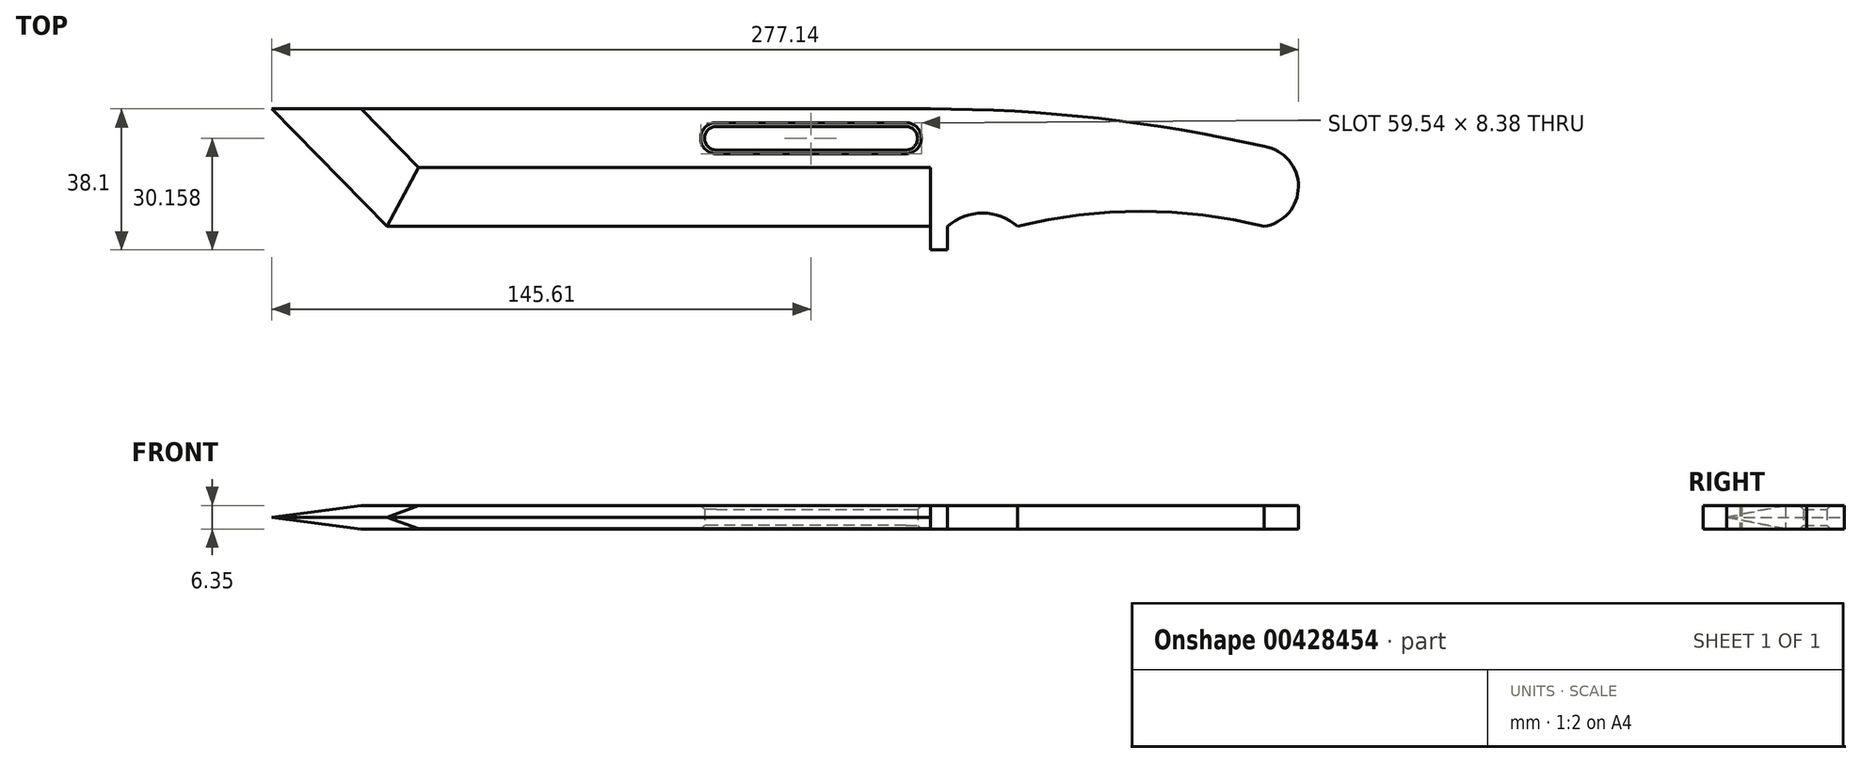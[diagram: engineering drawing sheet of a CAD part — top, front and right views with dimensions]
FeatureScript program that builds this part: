
annotation { "Feature Type Name" : "Feature", "Feature Type Description" : "" }
export const myFeature = defineFeature(function(context is Context, id is Id, definition is map)
    precondition{}
    {
        {
            var Q0;
            Q0=qCreatedBy(makeId("Top.planeOp"),FACE);
            var sketch = newSketch(context, id + "F0", { "sketchPlane" : qUnion([Q0])});
            skLineSegment(sketch, "E0", {"start": v(-135, 10.18) * mm, "end": v(-103.87, -21.57) * mm});
            skLineSegment(sketch, "E1", {"start": v(-135, 10.18) * mm, "end": v(42.8, 10.18) * mm});
            skLineSegment(sketch, "E2", {"start": v(-103.87, -21.57) * mm, "end": v(42.8, -21.57) * mm});
            skLineSegment(sketch, "E3", {"start": v(-103.87, -21.57) * mm, "end": v(-95.34, -5.7) * mm});
            skPoint(sketch, "E3.endSnap0", {"position": v(42.8, -5.7) * mm});
            skLineSegment(sketch, "E4", {"start": v(-95.34, -5.7) * mm, "end": v(42.8, -5.7) * mm});
            skLineSegment(sketch, "E5", {"start": v(-95.34, -5.7) * mm, "end": v(-110.83, 10.18) * mm});
            skLineSegment(sketch, "E6", {"start": v(42.8, -5.7) * mm, "end": v(42.8, -27.92) * mm});
            skLineSegment(sketch, "E7", {"start": v(42.8, -27.92) * mm, "end": v(47.45, -27.92) * mm});
            skLineSegment(sketch, "E8", {"start": v(47.45, -27.92) * mm, "end": v(47.45, -21.57) * mm});
            skArc(sketch, "E9", {"start": v(66.35, -21.57) * mm, "mid": v(56.9, -17.97) * mm, "end": v(47.45, -21.57) * mm});
            skArc(sketch, "E10", {"start": v(132.84, -21.57) * mm, "mid": v(99.6, -17.5) * mm, "end": v(66.35, -21.57) * mm});
            skArc(sketch, "E11", {"start": v(132.97, 0) * mm, "mid": v(88.17, 7.62) * mm, "end": v(42.8, 10.18) * mm});
            skArc(sketch, "E12", {"start": v(132.84, -21.57) * mm, "mid": v(142.14, -10.84) * mm, "end": v(132.97, 0) * mm});
            skLineSegment(sketch, "E13", {"start": v(36.19, 2.24) * mm, "end": v(-14.97, 2.24) * mm});
            skArc(sketch, "E14.0.startCap", {"start": v(36.19, 5.41) * mm, "mid": v(39.36, 2.24) * mm, "end": v(36.19, -0.94) * mm});
            skArc(sketch, "E14.0.endCap", {"start": v(-14.97, -0.94) * mm, "mid": v(-18.14, 2.24) * mm, "end": v(-14.97, 5.41) * mm});
            skLineSegment(sketch, "E14.0.left", {"start": v(36.19, -0.94) * mm, "end": v(-14.97, -0.94) * mm});
            skLineSegment(sketch, "E14.0.right", {"start": v(36.19, 5.41) * mm, "end": v(-14.97, 5.41) * mm});
            skSolve(sketch);
        }
        {
            var Q0;
            {var subQ6=sQuery(id+"F0.wireOp",EDGE,"E4");Q0=makeQuery(id+"F0.imprint","IMPRINT",FACE,{"disambiguationData":[TD([[makeQuery(id+"F0.imprint","IMPRINT",EDGE,{"derivedFrom":subQ6}),1.0]])]});}
            extrude(context, id + "F1", {"entities" : qUnion([Q0]), "depth" : 6.35 * mm});
        }
        {
            var Q0;
            {var subQ0=sQuery(id+"F0.wireOp",EDGE,"E2");Q0=makeQuery(id+"F0.imprint","IMPRINT",FACE,{"disambiguationData":[TD([[makeQuery(id+"F0.imprint","IMPRINT",EDGE,{"derivedFrom":subQ0}),1.0]])]});}
            extrude(context, id + "F2", {"entities" : qUnion([Q0]), "depth" : 6.35 * mm});
        }
        {
            var Q0;
            {var subQ0=sQuery(id+"F0.wireOp",EDGE,"E0");Q0=makeQuery(id+"F0.imprint","IMPRINT",FACE,{"disambiguationData":[TD([[makeQuery(id+"F0.imprint","IMPRINT",EDGE,{"derivedFrom":subQ0}),1.0]])]});}
            extrude(context, id + "F3", {"entities" : qUnion([Q0]), "depth" : 6.35 * mm});
        }
        {
            var Q0;
            Q0=makeQuery(id+"F2.opExtrude","CAP_EDGE",EDGE,{"disambiguationData":[OSD([sQuery(id+"F0.wireOp",EDGE,"E2")])],"isStart":false});
            var Q1;
            Q1=makeQuery(id+"F2.opExtrude","CAP_EDGE",EDGE,{"disambiguationData":[OSD([sQuery(id+"F0.wireOp",EDGE,"E2")])],"isStart":true});
            chamfer(context, id + "F4", {"entities" : qUnion([Q0, Q1]), "chamferType" : ChamferType.TWO_OFFSETS, "width1" : 16 * mm, "oppositeDirection" : false, "width2" : 3.17 * mm, "tangentPropagation" : true});
        }
        {
            var Q0;
            Q0=makeQuery(id+"F3.opExtrude","CAP_EDGE",EDGE,{"disambiguationData":[OSD([sQuery(id+"F0.wireOp",EDGE,"E0")])],"isStart":false});
            var Q1;
            Q1=makeQuery(id+"F3.opExtrude","CAP_EDGE",EDGE,{"disambiguationData":[OSD([sQuery(id+"F0.wireOp",EDGE,"E0")])],"isStart":true});
            chamfer(context, id + "F5", {"entities" : qUnion([Q0, Q1]), "chamferType" : ChamferType.TWO_OFFSETS, "width1" : 17.27 * mm, "oppositeDirection" : false, "width2" : 3.17 * mm, "tangentPropagation" : true});
        }
        {
            var Q0;
            Q0=makeQuery(id+"F1.opExtrude","CAP_EDGE",EDGE,{"disambiguationData":[OSD([sQuery(id+"F0.wireOp",EDGE,"E14.0.right")])],"isStart":false});
            var Q1;
            Q1=makeQuery(id+"F1.opExtrude","CAP_EDGE",EDGE,{"disambiguationData":[OSD([sQuery(id+"F0.wireOp",EDGE,"E14.0.endCap")])],"isStart":false});
            var Q2;
            Q2=makeQuery(id+"F1.opExtrude","CAP_EDGE",EDGE,{"disambiguationData":[OSD([sQuery(id+"F0.wireOp",EDGE,"E14.0.left")])],"isStart":false});
            var Q3;
            Q3=makeQuery(id+"F1.opExtrude","CAP_EDGE",EDGE,{"disambiguationData":[OSD([sQuery(id+"F0.wireOp",EDGE,"E14.0.startCap")])],"isStart":false});
            var Q4;
            Q4=makeQuery(id+"F1.opExtrude","CAP_EDGE",EDGE,{"disambiguationData":[OSD([sQuery(id+"F0.wireOp",EDGE,"E14.0.left")])],"isStart":true});
            var Q5;
            Q5=makeQuery(id+"F1.opExtrude","CAP_EDGE",EDGE,{"disambiguationData":[OSD([sQuery(id+"F0.wireOp",EDGE,"E14.0.endCap")])],"isStart":true});
            var Q6;
            Q6=makeQuery(id+"F1.opExtrude","CAP_EDGE",EDGE,{"disambiguationData":[OSD([sQuery(id+"F0.wireOp",EDGE,"E14.0.startCap")])],"isStart":true});
            chamfer(context, id + "F6", {"entities" : qUnion([Q0, Q1, Q2, Q3, Q4, Q5, Q6]), "width" : 1.02 * mm, "tangentPropagation" : true});
        }
    });
